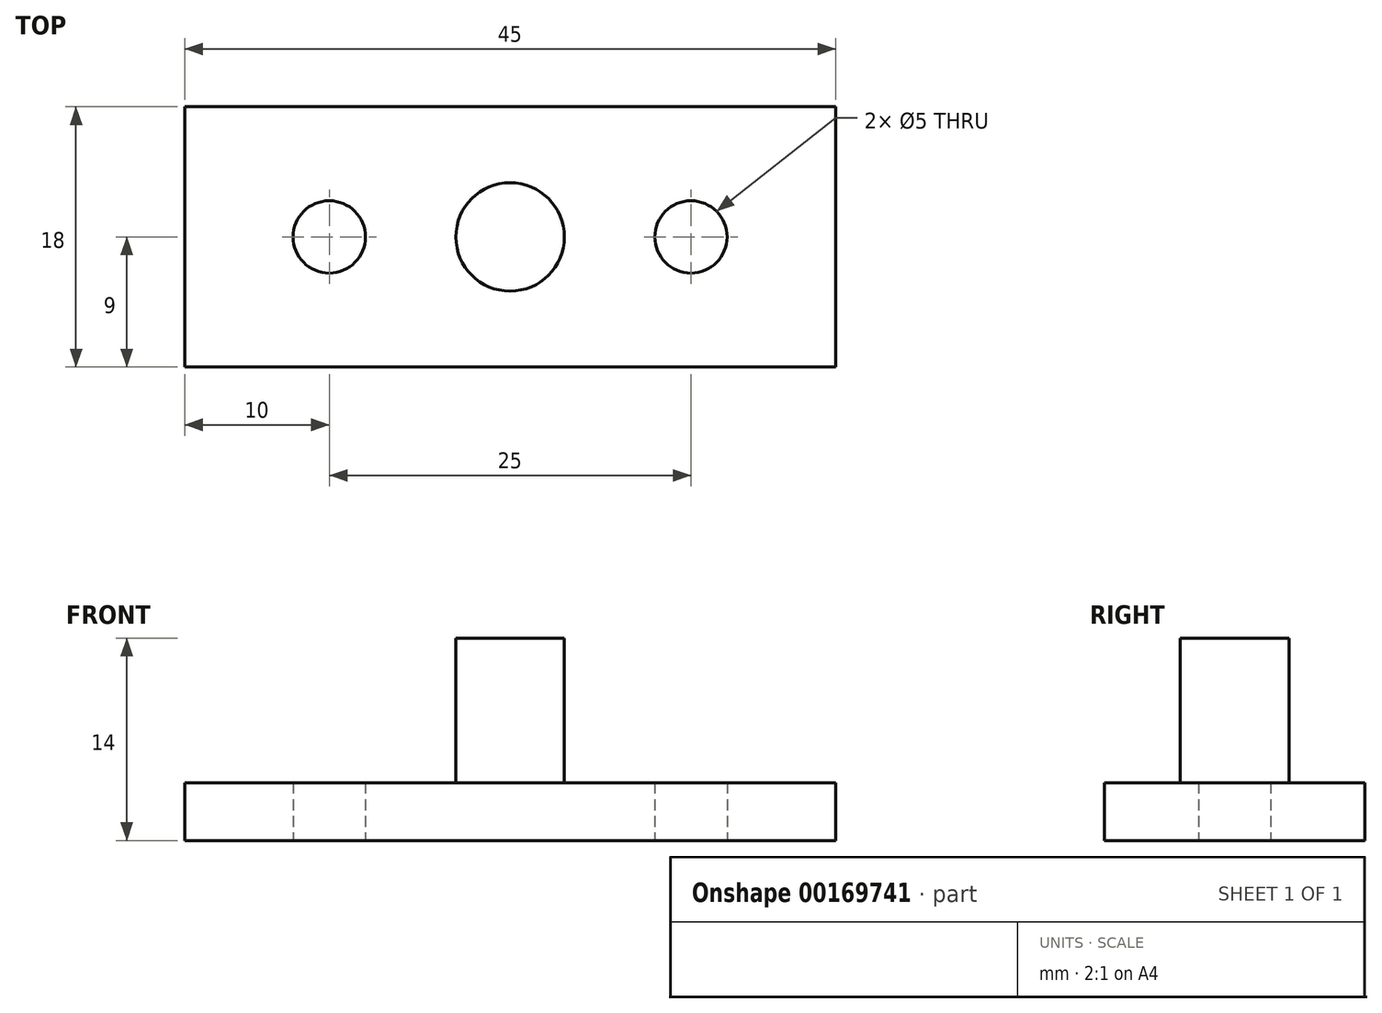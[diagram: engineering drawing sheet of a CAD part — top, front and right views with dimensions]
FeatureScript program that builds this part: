
annotation { "Feature Type Name" : "Feature", "Feature Type Description" : "" }
export const myFeature = defineFeature(function(context is Context, id is Id, definition is map)
    precondition{}
    {
        {
            var Q0;
            Q0=qCreatedBy(makeId("Top.planeOp"),FACE);
            var sketch = newSketch(context, id + "F0", { "sketchPlane" : qUnion([Q0])});
            skLineSegment(sketch, "E0.bottom", {"start": v(22.5, -9) * mm, "end": v(-22.5, -9) * mm});
            skLineSegment(sketch, "E0.top", {"start": v(22.5, 9) * mm, "end": v(-22.5, 9) * mm});
            skLineSegment(sketch, "E0.left", {"start": v(22.5, -9) * mm, "end": v(22.5, 9) * mm});
            skLineSegment(sketch, "E0.right", {"start": v(-22.5, -9) * mm, "end": v(-22.5, 9) * mm});
            skPoint(sketch, "E0.middle", {"position": v(0, 0) * mm});
            skCircle(sketch, "E1", {"center": v(-12.5, 0) * mm, "radius": 2.5 * mm});
            skCircle(sketch, "E2", {"center": v(12.5, 0) * mm, "radius": 2.5 * mm});
            skSolve(sketch);
        }
        {
            var Q0;
            Q0=makeQuery(id+"F0.imprint","IMPRINT",FACE,{"disambiguationData":[TD([[makeQuery(id+"F0.imprint","IMPRINT",EDGE,{"derivedFrom":sQuery(id+"F0.wireOp",EDGE,"E0.bottom")}),-1.0]])]});
            extrude(context, id + "F1", {"entities" : qUnion([Q0]), "depth" : 4 * mm});
        }
        {
            var Q0;
            Q0=makeQuery(id+"F1.opExtrude","CAP_FACE",FACE,{"disambiguationData":[OSD([sQuery(id+"F0.wireOp",EDGE,"E0.bottom"),sQuery(id+"F0.wireOp",EDGE,"E0.top"),sQuery(id+"F0.wireOp",EDGE,"E0.left"),sQuery(id+"F0.wireOp",EDGE,"E0.right"),sQuery(id+"F0.wireOp",EDGE,"E1"),sQuery(id+"F0.wireOp",EDGE,"E2")])],"isStart":false});
            var sketch = newSketch(context, id + "F2", { "sketchPlane" : qUnion([Q0])});
            skCircle(sketch, "E3", {"center": v(0, 0) * mm, "radius": 3.75 * mm});
            skSolve(sketch);
        }
        {
            var Q0;
            Q0=makeQuery(id+"F2.imprint","IMPRINT",FACE,{"disambiguationData":[TD([[makeQuery(id+"F2.imprint","IMPRINT",EDGE,{"derivedFrom":sQuery(id+"F2.wireOp",EDGE,"E3")}),1.0]])]});
            extrude(context, id + "F3", {"entities" : qUnion([Q0]), "operationType" : NewBodyOperationType.ADD, "depth" : 10 * mm});
        }
    });
